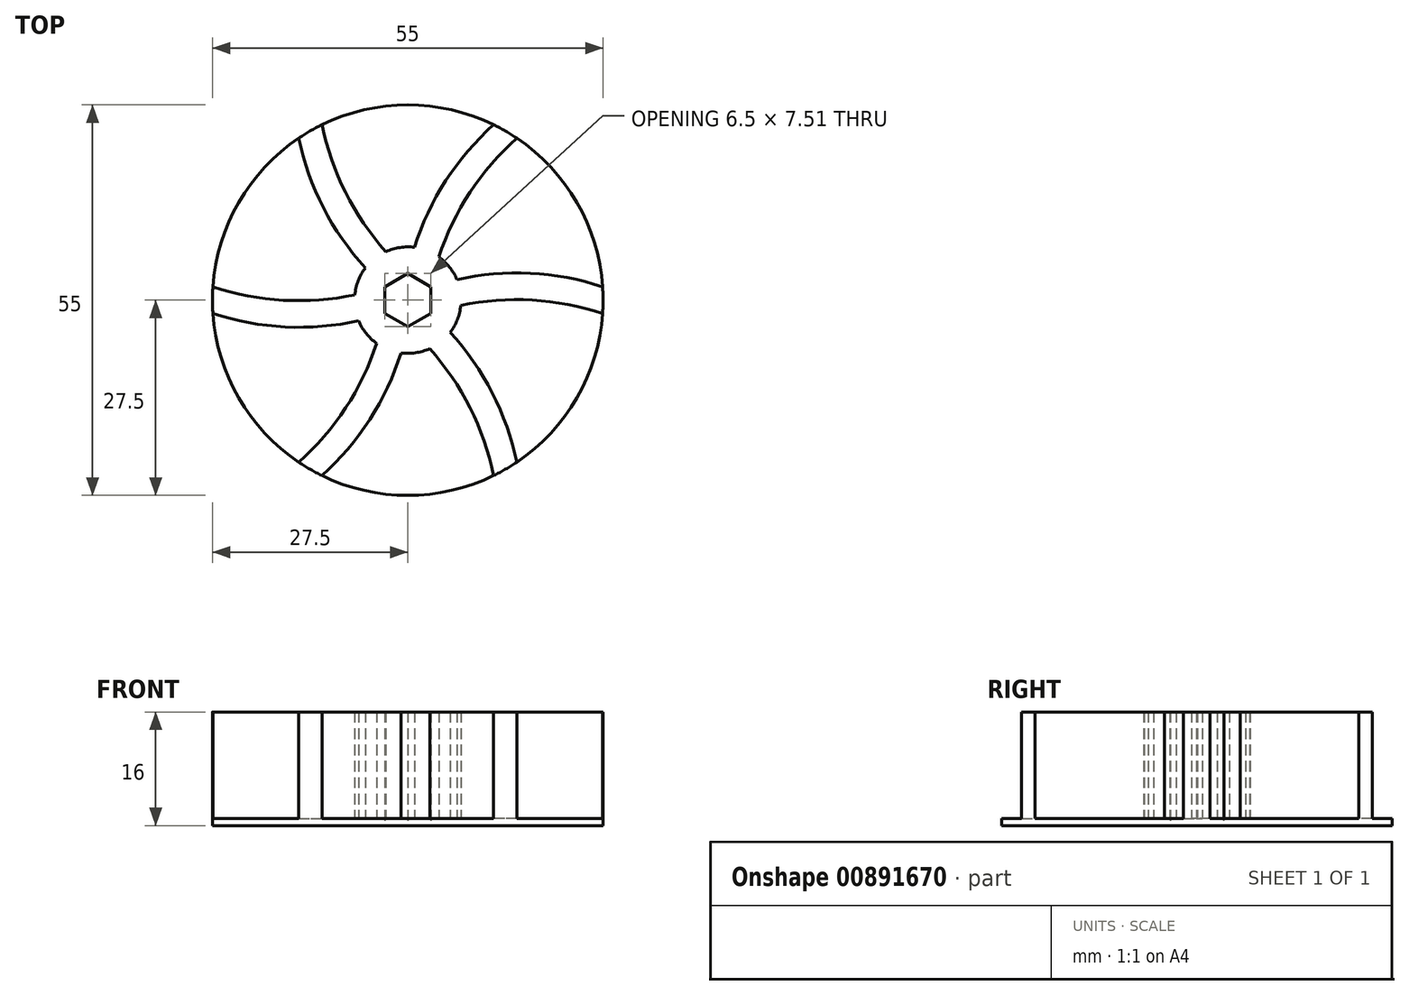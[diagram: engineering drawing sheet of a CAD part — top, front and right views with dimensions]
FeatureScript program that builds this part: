
annotation { "Feature Type Name" : "Feature", "Feature Type Description" : "" }
export const myFeature = defineFeature(function(context is Context, id is Id, definition is map)
    precondition{}
    {
        {
            var Q0;
            Q0=qCreatedBy(makeId("Top.planeOp"),FACE);
            var sketch = newSketch(context, id + "F0", { "sketchPlane" : qUnion([Q0])});
            skCircle(sketch, "E0", {"center": v(0, 0) * mm, "radius": 27.5 * mm});
            skCircle(sketch, "E1.cCircle", {"center": v(0, 0) * mm, "radius": 3.75 * mm, "construction": true});
            skLineSegment(sketch, "E1.0", {"start": v(0, 3.75) * mm, "end": v(3.25, 1.88) * mm});
            skLineSegment(sketch, "E1.1", {"start": v(3.25, 1.88) * mm, "end": v(3.25, -1.88) * mm});
            skLineSegment(sketch, "E1.2", {"start": v(3.25, -1.88) * mm, "end": v(0, -3.75) * mm});
            skLineSegment(sketch, "E1.3", {"start": v(0, -3.75) * mm, "end": v(-3.25, -1.88) * mm});
            skLineSegment(sketch, "E1.4", {"start": v(-3.25, -1.88) * mm, "end": v(-3.25, 1.88) * mm});
            skLineSegment(sketch, "E1.5", {"start": v(-3.25, 1.88) * mm, "end": v(0, 3.75) * mm});
            skCircle(sketch, "E2", {"center": v(0, 0) * mm, "radius": 7.5 * mm});
            skSolve(sketch);
        }
        {
            var Q0;
            Q0=makeQuery(id+"F0.imprint","IMPRINT",FACE,{"disambiguationData":[TD([[makeQuery(id+"F0.imprint","IMPRINT",EDGE,{"derivedFrom":sQuery(id+"F0.wireOp",EDGE,"E0")}),1.0]])]});
            var Q1;
            Q1=makeQuery(id+"F0.imprint","IMPRINT",FACE,{"disambiguationData":[TD([[makeQuery(id+"F0.imprint","IMPRINT",EDGE,{"derivedFrom":sQuery(id+"F0.wireOp",EDGE,"E1.0")}),1.0]])]});
            extrude(context, id + "F1", {"entities" : qUnion([Q0, Q1]), "depth" : 1 * mm, "offsetDistance" : 25 * mm});
        }
        {
            var Q0;
            Q0=makeQuery(id+"F1.opExtrude","CAP_FACE",FACE,{"disambiguationData":[OSD([sQuery(id+"F0.wireOp",EDGE,"E0"),sQuery(id+"F0.wireOp",EDGE,"E1.0"),sQuery(id+"F0.wireOp",EDGE,"E1.1"),sQuery(id+"F0.wireOp",EDGE,"E1.2"),sQuery(id+"F0.wireOp",EDGE,"E1.3"),sQuery(id+"F0.wireOp",EDGE,"E1.4"),sQuery(id+"F0.wireOp",EDGE,"E1.5")])],"isStart":false});
            var sketch = newSketch(context, id + "F2", { "sketchPlane" : qUnion([Q0])});
            skPoint(sketch, "E3.startSnap0", {"position": v(-3.25, 0) * mm});
            skArc(sketch, "E4", {"start": v(-27.44, -1.88) * mm, "mid": v(-15.34, -3.82) * mm, "end": v(-3.25, -1.88) * mm});
            skArc(sketch, "E5", {"start": v(-27.44, 1.88) * mm, "mid": v(-15.34, -0.07) * mm, "end": v(-3.25, 1.88) * mm});
            skArc(sketch, "E6", {"start": v(27.44, 1.88) * mm, "mid": v(15.34, 3.82) * mm, "end": v(3.25, 1.88) * mm});
            skArc(sketch, "E7", {"start": v(27.44, -1.88) * mm, "mid": v(15.34, 0.07) * mm, "end": v(3.25, -1.88) * mm});
            skSolve(sketch);
        }
        {
            var Q0;
            Q0 = qSketchRegion(id + "F2", true);
            var Q1;
            {var subQ0=sQuery(id+"F2.wireOp",EDGE,"E4");Q1=makeQuery(id+"F2.imprint","IMPRINT",FACE,{"disambiguationData":[TD([[makeQuery(id+"F2.imprint","IMPRINT",EDGE,{"derivedFrom":subQ0}),1.0]])]});}
            var Q2;
            {var subQ0=sQuery(id+"F2.wireOp",EDGE,"E6");Q2=makeQuery(id+"F2.imprint","IMPRINT",FACE,{"disambiguationData":[TD([[makeQuery(id+"F2.imprint","IMPRINT",EDGE,{"derivedFrom":subQ0}),1.0]])]});}
            extrude(context, id + "F3", {"entities" : qUnion([Q0, Q1, Q2]), "operationType" : NewBodyOperationType.ADD, "depth" : 15 * mm, "offsetDistance" : 25 * mm});
        }
        {
            var Q0;
            Q0=makeQuery(id+"F1.opExtrude","SWEPT_BODY",BODY,{"disambiguationData":[OSD([sQuery(id+"F0.wireOp",EDGE,"E0"),sQuery(id+"F0.wireOp",EDGE,"E1.0"),sQuery(id+"F0.wireOp",EDGE,"E1.1"),sQuery(id+"F0.wireOp",EDGE,"E1.2"),sQuery(id+"F0.wireOp",EDGE,"E1.3"),sQuery(id+"F0.wireOp",EDGE,"E1.4"),sQuery(id+"F0.wireOp",EDGE,"E1.5")])]});
            var Q1;
            {var subQ0=sQuery(id+"F2.wireOp",EDGE,"E4");var subQ1=sQuery(id+"F0.wireOp",EDGE,"E0");var subQ2=makeQuery(id+"F1.opExtrude","CAP_EDGE",EDGE,{"disambiguationData":[OSD([subQ1])],"isStart":false});Q1=makeQuery(id+"F3.boolean.opBoolean","SPLIT",EDGE,{"disambiguationData":[TD([makeQuery(id+"F3.opExtrude","SWEPT_FACE",FACE,{"disambiguationData":[OSD([subQ0])]})])],"derivedFrom":subQ2});}
            circularPattern(context, id + "F4", {"entities" : qUnion([Q0]), "axis" : qUnion([Q1]), "angle" : 360 * degree, "instanceCount" : 6, "equalSpace" : true});
        }
        {
            var Q0;
            Q0=makeQuery(id+"F0.imprint","IMPRINT",FACE,{"disambiguationData":[TD([[makeQuery(id+"F0.imprint","IMPRINT",EDGE,{"derivedFrom":sQuery(id+"F0.wireOp",EDGE,"E1.0")}),1.0]])]});
            extrude(context, id + "F5", {"entities" : qUnion([Q0]), "operationType" : NewBodyOperationType.ADD, "depth" : 16 * mm, "offsetDistance" : 25 * mm});
        }
    });
